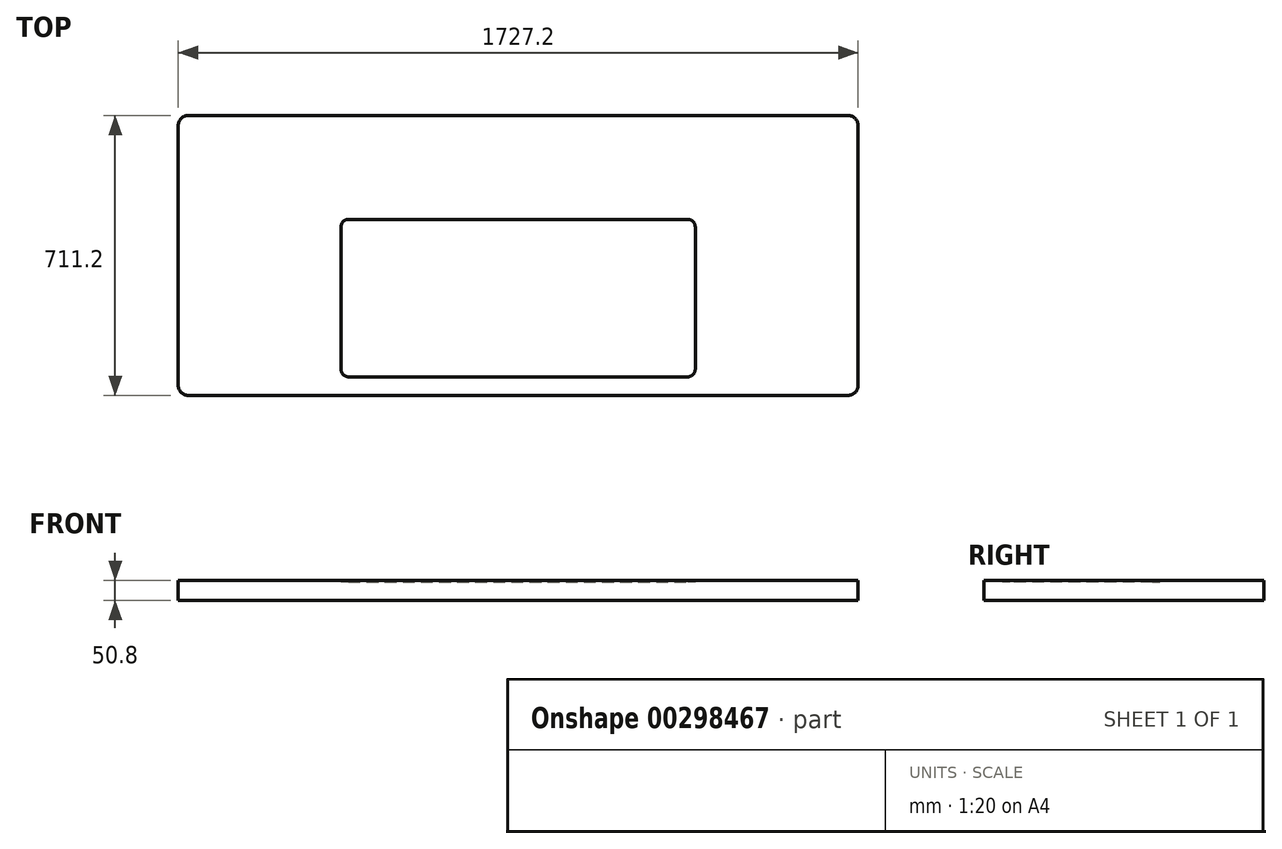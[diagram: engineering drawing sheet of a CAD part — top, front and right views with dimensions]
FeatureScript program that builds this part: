
annotation { "Feature Type Name" : "Feature", "Feature Type Description" : "" }
export const myFeature = defineFeature(function(context is Context, id is Id, definition is map)
    precondition{}
    {
        {
            var Q0;
            Q0=qCreatedBy(makeId("Top.planeOp"),FACE);
            var sketch = newSketch(context, id + "F0", { "sketchPlane" : qUnion([Q0])});
            skLineSegment(sketch, "E0.bottom", {"start": v(-838.2, 355.6) * mm, "end": v(838.2, 355.6) * mm});
            skLineSegment(sketch, "E0.top", {"start": v(-838.2, -355.6) * mm, "end": v(838.2, -355.6) * mm});
            skLineSegment(sketch, "E0.left", {"start": v(-863.6, 330.2) * mm, "end": v(-863.6, -330.2) * mm});
            skLineSegment(sketch, "E0.right", {"start": v(863.6, 330.2) * mm, "end": v(863.6, -330.2) * mm});
            skPoint(sketch, "E0.middle", {"position": v(0, 0) * mm});
            skPoint(sketch, "E1.visualSharp", {"position": v(-863.6, 355.6) * mm});
            skArc(sketch, "E1.filletArc", {"start": v(-838.2, 355.6) * mm, "mid": v(-856.16, 348.16) * mm, "end": v(-863.6, 330.2) * mm});
            skPoint(sketch, "E2.visualSharp", {"position": v(863.6, 355.6) * mm});
            skArc(sketch, "E2.filletArc", {"start": v(863.6, 330.2) * mm, "mid": v(856.16, 348.16) * mm, "end": v(838.2, 355.6) * mm});
            skPoint(sketch, "E3.visualSharp", {"position": v(863.6, -355.6) * mm});
            skArc(sketch, "E3.filletArc", {"start": v(838.2, -355.6) * mm, "mid": v(856.16, -348.16) * mm, "end": v(863.6, -330.2) * mm});
            skPoint(sketch, "E4.visualSharp", {"position": v(-863.6, -355.6) * mm});
            skArc(sketch, "E4.filletArc", {"start": v(-863.6, -330.2) * mm, "mid": v(-856.16, -348.16) * mm, "end": v(-838.2, -355.6) * mm});
            skSolve(sketch);
        }
        {
            var Q0;
            Q0=makeQuery(id+"F0.imprint","IMPRINT",FACE,{"disambiguationData":[TD([[makeQuery(id+"F0.imprint","IMPRINT",EDGE,{"derivedFrom":sQuery(id+"F0.wireOp",EDGE,"E0.bottom")}),-1.0]])]});
            extrude(context, id + "F1", {"entities" : qUnion([Q0]), "depth" : 50.8 * mm});
        }
        {
            var Q0;
            Q0=makeQuery(id+"F1.opExtrude","CAP_FACE",FACE,{"disambiguationData":[OSD([sQuery(id+"F0.wireOp",EDGE,"E0.bottom"),sQuery(id+"F0.wireOp",EDGE,"E0.top"),sQuery(id+"F0.wireOp",EDGE,"E0.left"),sQuery(id+"F0.wireOp",EDGE,"E0.right"),sQuery(id+"F0.wireOp",EDGE,"E1.filletArc"),sQuery(id+"F0.wireOp",EDGE,"E2.filletArc"),sQuery(id+"F0.wireOp",EDGE,"E3.filletArc"),sQuery(id+"F0.wireOp",EDGE,"E4.filletArc")])],"isStart":false});
            var sketch = newSketch(context, id + "F2", { "sketchPlane" : qUnion([Q0])});
            skLineSegment(sketch, "E5.bottom", {"start": v(-430.95, 91.7) * mm, "end": v(430.95, 91.7) * mm});
            skLineSegment(sketch, "E5.top", {"start": v(-430.95, -308.29) * mm, "end": v(430.95, -308.29) * mm});
            skLineSegment(sketch, "E5.left", {"start": v(-450, 72.66) * mm, "end": v(-450, -289.24) * mm});
            skLineSegment(sketch, "E5.right", {"start": v(450, 72.66) * mm, "end": v(450, -289.24) * mm});
            skPoint(sketch, "E5.middle", {"position": v(0, -108.29) * mm});
            skPoint(sketch, "E6", {"position": v(0, -355.6) * mm});
            skPoint(sketch, "E7.visualSharp", {"position": v(-450, 91.7) * mm});
            skArc(sketch, "E7.filletArc", {"start": v(-430.95, 91.7) * mm, "mid": v(-444.42, 86.13) * mm, "end": v(-450, 72.66) * mm});
            skPoint(sketch, "E8.visualSharp", {"position": v(450, 91.7) * mm});
            skArc(sketch, "E8.filletArc", {"start": v(450, 72.66) * mm, "mid": v(444.42, 86.13) * mm, "end": v(430.95, 91.7) * mm});
            skPoint(sketch, "E9.visualSharp", {"position": v(450, -308.29) * mm});
            skArc(sketch, "E9.filletArc", {"start": v(430.95, -308.29) * mm, "mid": v(444.42, -302.7) * mm, "end": v(450, -289.24) * mm});
            skPoint(sketch, "E10.visualSharp", {"position": v(-450, -308.29) * mm});
            skArc(sketch, "E10.filletArc", {"start": v(-450, -289.24) * mm, "mid": v(-444.42, -302.7) * mm, "end": v(-430.95, -308.29) * mm});
            skSolve(sketch);
        }
        {
            var Q0;
            Q0=makeQuery(id+"F2.imprint","IMPRINT",FACE,{"disambiguationData":[TD([[makeQuery(id+"F2.imprint","IMPRINT",EDGE,{"derivedFrom":sQuery(id+"F2.wireOp",EDGE,"E5.bottom")}),-1.0]])]});
            extrude(context, id + "F3", {"entities" : qUnion([Q0]), "operationType" : NewBodyOperationType.REMOVE, "oppositeDirection" : true, "depth" : 4 * mm});
        }
    });
